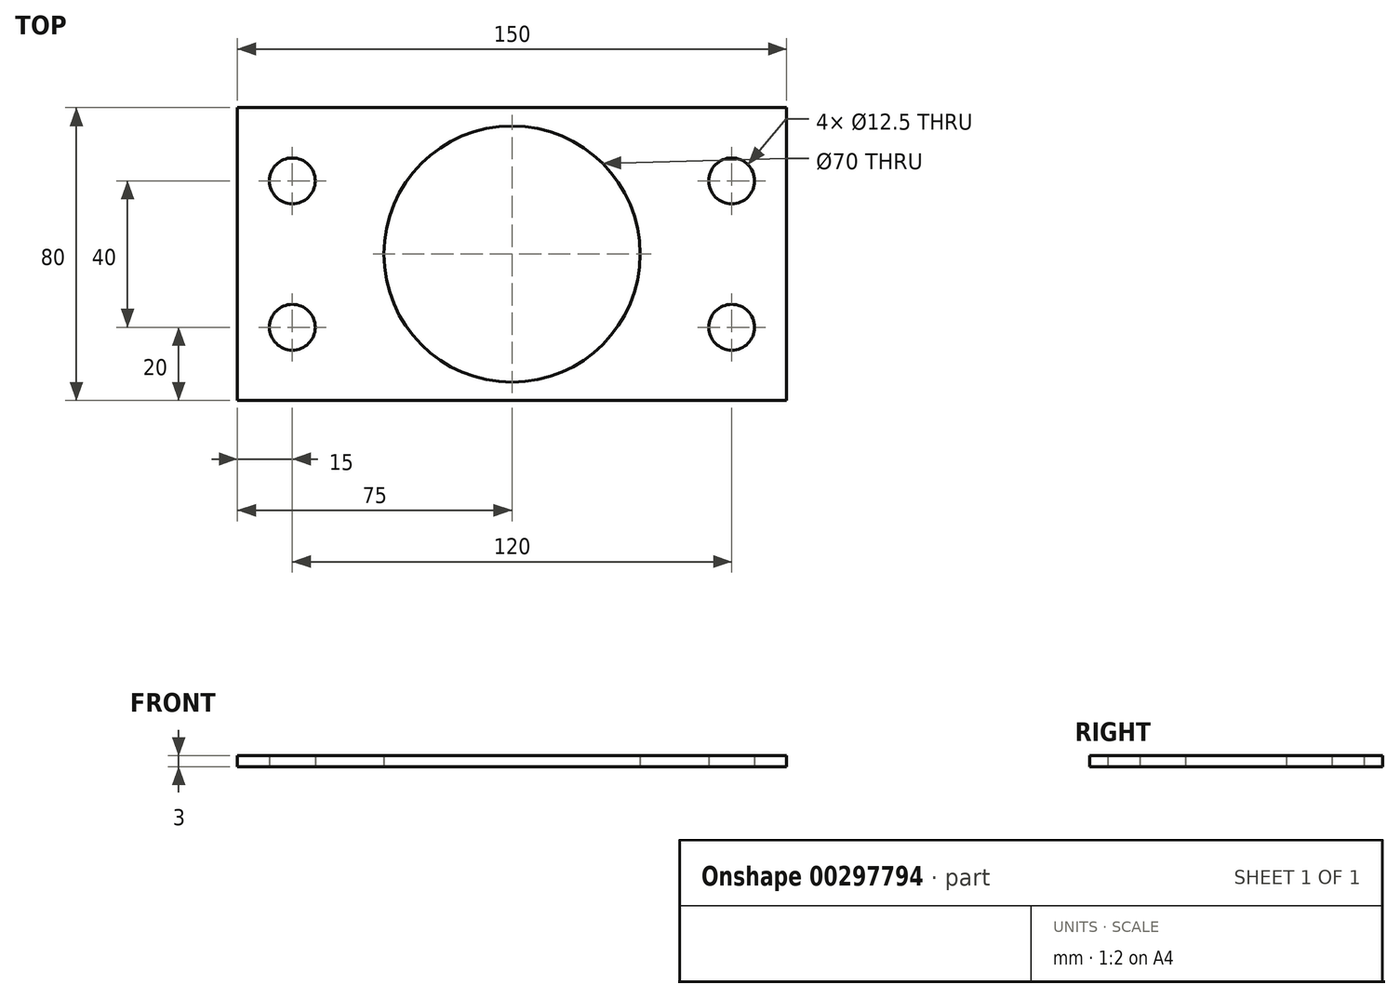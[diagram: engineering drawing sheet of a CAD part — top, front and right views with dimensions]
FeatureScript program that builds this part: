
annotation { "Feature Type Name" : "Feature", "Feature Type Description" : "" }
export const myFeature = defineFeature(function(context is Context, id is Id, definition is map)
    precondition{}
    {
        {
            var Q0;
            Q0=qCreatedBy(makeId("Top.planeOp"),FACE);
            var sketch = newSketch(context, id + "F0", { "sketchPlane" : qUnion([Q0])});
            skLineSegment(sketch, "E0.bottom", {"start": v(75, 40) * mm, "end": v(-75, 40) * mm});
            skLineSegment(sketch, "E0.top", {"start": v(75, -40) * mm, "end": v(-75, -40) * mm});
            skLineSegment(sketch, "E0.left", {"start": v(75, 40) * mm, "end": v(75, -40) * mm});
            skLineSegment(sketch, "E0.right", {"start": v(-75, 40) * mm, "end": v(-75, -40) * mm});
            skPoint(sketch, "E0.middle", {"position": v(0, 0) * mm});
            skCircle(sketch, "E1", {"center": v(0, 0) * mm, "radius": 35 * mm});
            skCircle(sketch, "E2", {"center": v(-60, 20) * mm, "radius": 6.25 * mm});
            skCircle(sketch, "E3.0.1.0", {"center": v(-60, -20) * mm, "radius": 6.25 * mm});
            skCircle(sketch, "E3.1.0.0", {"center": v(60, 20) * mm, "radius": 6.25 * mm});
            skCircle(sketch, "E3.1.1.0", {"center": v(60, -20) * mm, "radius": 6.25 * mm});
            skLineSegment(sketch, "E3.direction1", {"start": v(-60, 20) * mm, "end": v(60, 20) * mm, "construction": true});
            skLineSegment(sketch, "E3.direction2", {"start": v(-60, 20) * mm, "end": v(-60, -20) * mm, "construction": true});
            skSolve(sketch);
        }
        {
            var Q0;
            Q0 = qSketchRegion(id + "F0", true);
            extrude(context, id + "F1", {"entities" : qUnion([Q0]), "depth" : 3 * mm});
        }
    });
